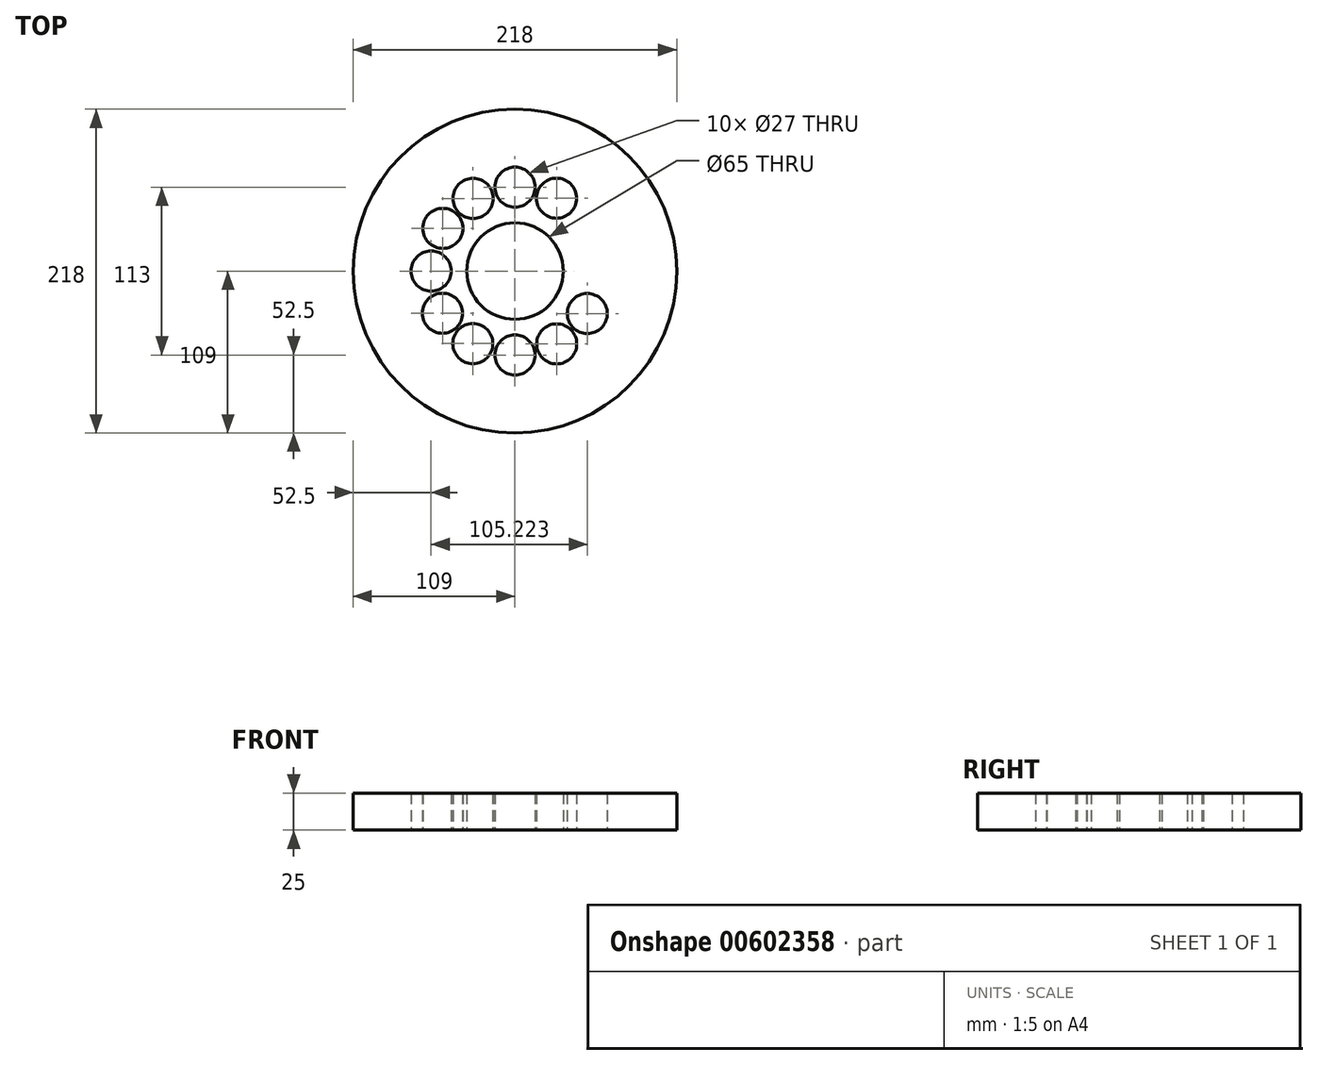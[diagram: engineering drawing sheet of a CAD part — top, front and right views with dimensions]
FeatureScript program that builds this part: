
annotation { "Feature Type Name" : "Feature", "Feature Type Description" : "" }
export const myFeature = defineFeature(function(context is Context, id is Id, definition is map)
    precondition{}
    {
        {
            var Q0;
            Q0=qCreatedBy(makeId("Top.planeOp"),FACE);
            var sketch = newSketch(context, id + "F0", { "sketchPlane" : qUnion([Q0])});
            skCircle(sketch, "E0", {"center": v(0, 0) * mm, "radius": 109 * mm});
            skCircle(sketch, "E1", {"center": v(0, 0) * mm, "radius": 75 * mm});
            skCircle(sketch, "E2", {"center": v(0, 0) * mm, "radius": 37.5 * mm});
            skCircle(sketch, "E3", {"center": v(0, 0) * mm, "radius": 32.5 * mm});
            skPoint(sketch, "E4.start.orphan", {"position": v(0, 109) * mm});
            skPoint(sketch, "E5.start.orphan", {"position": v(0, -109) * mm});
            skCircle(sketch, "E6", {"center": v(0, 56.5) * mm, "radius": 13.5 * mm});
            skCircle(sketch, "E7", {"center": v(0, -56.5) * mm, "radius": 13.5 * mm});
            skCircle(sketch, "E8", {"center": v(-56.5, 0) * mm, "radius": 13.5 * mm});
            skCircle(sketch, "E9", {"center": v(28.1, -49.02) * mm, "radius": 13.5 * mm});
            skCircle(sketch, "E10", {"center": v(48.72, -28.6) * mm, "radius": 13.5 * mm});
            skCircle(sketch, "E11", {"center": v(-48.85, -28.4) * mm, "radius": 13.5 * mm});
            skCircle(sketch, "E12", {"center": v(-28.4, -48.84) * mm, "radius": 13.5 * mm});
            skCircle(sketch, "E13", {"center": v(-48.62, 28.77) * mm, "radius": 13.5 * mm});
            skCircle(sketch, "E14", {"center": v(-28.23, 48.94) * mm, "radius": 13.5 * mm});
            skCircle(sketch, "E15", {"center": v(28.01, 49.07) * mm, "radius": 13.5 * mm});
            skSolve(sketch);
        }
        {
            var Q0;
            Q0 = qSketchRegion(id + "F0", true);
            var Q1;
            Q1=makeQuery(id+"F0.imprint","IMPRINT",FACE,{"disambiguationData":[TD([[makeQuery(id+"F0.imprint","IMPRINT",EDGE,{"derivedFrom":sQuery(id+"F0.wireOp",EDGE,"E1")}),1.0]])]});
            var Q2;
            Q2=makeQuery(id+"F0.imprint","IMPRINT",FACE,{"disambiguationData":[TD([[makeQuery(id+"F0.imprint","IMPRINT",EDGE,{"derivedFrom":sQuery(id+"F0.wireOp",EDGE,"E2")}),1.0]])]});
            extrude(context, id + "F1", {"entities" : qUnion([Q0, Q1, Q2]), "depth" : 25 * mm, "offsetDistance" : 25 * mm});
        }
    });
